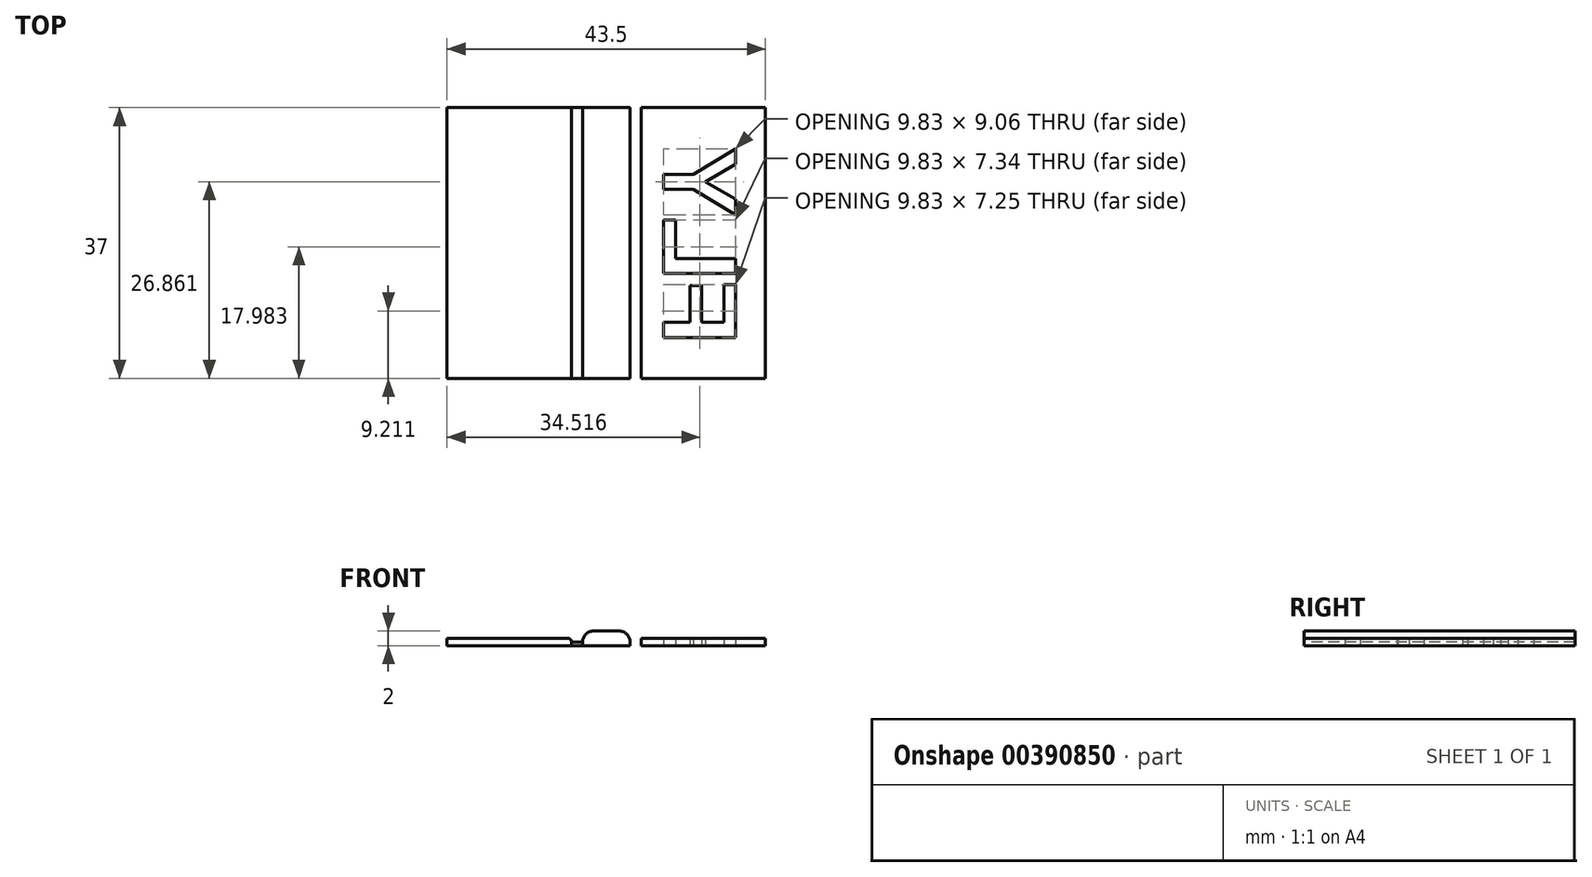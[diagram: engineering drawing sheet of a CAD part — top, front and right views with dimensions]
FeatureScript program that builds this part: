
annotation { "Feature Type Name" : "Feature", "Feature Type Description" : "" }
export const myFeature = defineFeature(function(context is Context, id is Id, definition is map)
    precondition{}
    {
        {
            var Q0;
            Q0=qCreatedBy(makeId("Top.planeOp"),FACE);
            var sketch = newSketch(context, id + "F0", { "sketchPlane" : qUnion([Q0])});
            skLineSegment(sketch, "E0.bottom", {"start": v(-8.5, -18.5) * mm, "end": v(8.5, -18.5) * mm});
            skLineSegment(sketch, "E0.top", {"start": v(-8.5, 18.5) * mm, "end": v(8.5, 18.5) * mm});
            skLineSegment(sketch, "E0.left", {"start": v(-8.5, -18.5) * mm, "end": v(-8.5, 18.5) * mm});
            skLineSegment(sketch, "E0.right", {"start": v(8.5, -18.5) * mm, "end": v(8.5, 18.5) * mm});
            skPoint(sketch, "E0.middle", {"position": v(0, 0) * mm});
            skLineSegment(sketch, "E1.bottom", {"start": v(-8.5, 18.5) * mm, "end": v(-16.5, 18.5) * mm});
            skLineSegment(sketch, "E1.top", {"start": v(-8.5, -18.5) * mm, "end": v(-16.5, -18.5) * mm});
            skLineSegment(sketch, "E1.left", {"start": v(-8.5, 18.5) * mm, "end": v(-8.5, -18.5) * mm});
            skLineSegment(sketch, "E1.right", {"start": v(-16.5, 18.5) * mm, "end": v(-16.5, -18.5) * mm});
            skLineSegment(sketch, "E2", {"start": v(-10, 18.5) * mm, "end": v(-10, -18.5) * mm});
            skLineSegment(sketch, "E3", {"start": v(-16.5, 18.5) * mm, "end": v(-35, 18.5) * mm});
            skLineSegment(sketch, "E4", {"start": v(-35, 18.5) * mm, "end": v(-35, -18.5) * mm});
            skLineSegment(sketch, "E5", {"start": v(-35, -18.5) * mm, "end": v(-16.5, -18.5) * mm});
            skLineSegment(sketch, "E6", {"start": v(-18, 18.5) * mm, "end": v(-18, -18.5) * mm});
            skSolve(sketch);
        }
        {
            var Q0;
            Q0=makeQuery(id+"F0.imprint","IMPRINT",FACE,{"disambiguationData":[TD([[makeQuery(id+"F0.imprint","IMPRINT",EDGE,{"derivedFrom":sQuery(id+"F0.wireOp",EDGE,"E0.bottom")}),1.0]])]});
            var Q1;
            {var subQ0=sQuery(id+"F0.wireOp",EDGE,"E4");Q1=makeQuery(id+"F0.imprint","IMPRINT",FACE,{"disambiguationData":[TD([[makeQuery(id+"F0.imprint","IMPRINT",EDGE,{"derivedFrom":subQ0}),1.0]])]});}
            extrude(context, id + "F1", {"entities" : qUnion([Q0, Q1]), "depth" : 1 * mm, "offsetDistance" : 25 * mm});
        }
        {
            var Q0;
            {var subQ0=sQuery(id+"F0.wireOp",EDGE,"E1.right");Q0=makeQuery(id+"F0.imprint","IMPRINT",FACE,{"disambiguationData":[TD([[makeQuery(id+"F0.imprint","IMPRINT",EDGE,{"derivedFrom":subQ0}),1.0]])]});}
            extrude(context, id + "F2", {"entities" : qUnion([Q0]), "depth" : 2 * mm, "offsetDistance" : 25 * mm});
        }
        {
            var Q0;
            {var subQ0=sQuery(id+"F0.wireOp",EDGE,"E1.right");Q0=makeQuery(id+"F0.imprint","IMPRINT",FACE,{"disambiguationData":[TD([[makeQuery(id+"F0.imprint","IMPRINT",EDGE,{"derivedFrom":subQ0}),-1.0]])]});}
            var Q1;
            {var subQ0=sQuery(id+"F0.wireOp",EDGE,"E1.left");Q1=makeQuery(id+"F0.imprint","IMPRINT",FACE,{"disambiguationData":[TD([[makeQuery(id+"F0.imprint","IMPRINT",EDGE,{"derivedFrom":subQ0}),-1.0]])]});}
            extrude(context, id + "F3", {"entities" : qUnion([Q0, Q1]), "depth" : .5 * mm, "offsetDistance" : 25 * mm});
        }
        {
            var Q0;
            Q0=makeQuery(id+"F2.opExtrude","CAP_EDGE",EDGE,{"disambiguationData":[OSD([sQuery(id+"F0.wireOp",EDGE,"E2")])],"isStart":false});
            var Q1;
            Q1=makeQuery(id+"F2.opExtrude","CAP_EDGE",EDGE,{"disambiguationData":[OSD([sQuery(id+"F0.wireOp",EDGE,"E1.right")])],"isStart":false});
            fillet(context, id + "F4", {"entities" : qUnion([Q0, Q1]), "radius" : 1.5 * mm, "tangentPropagation" : true, "allowEdgeOverflow" : false});
        }
        {
            var Q0;
            Q0=makeQuery(id+"F1.opExtrude","CAP_EDGE",EDGE,{"disambiguationData":[OSD([sQuery(id+"F0.wireOp",EDGE,"E6")])],"isStart":false});
            var Q1;
            Q1=makeQuery(id+"F1.opExtrude","CAP_EDGE",EDGE,{"disambiguationData":[OSD([sQuery(id+"F0.wireOp",EDGE,"E1.left")])],"isStart":false});
            fillet(context, id + "F5", {"entities" : qUnion([Q0, Q1]), "radius" : .5 * mm, "tangentPropagation" : true, "allowEdgeOverflow" : false});
        }
        {
            var Q0;
            Q0=makeQuery(id+"F1.opExtrude","CAP_FACE",FACE,{"disambiguationData":[OSD([sQuery(id+"F0.wireOp",EDGE,"E0.bottom"),sQuery(id+"F0.wireOp",EDGE,"E0.top"),sQuery(id+"F0.wireOp",EDGE,"E0.right"),sQuery(id+"F0.wireOp",EDGE,"E1.left")])],"isStart":true});
            var sketch = newSketch(context, id + "F6", { "sketchPlane" : qUnion([Q0])});
            skText(sketch, "E7", { "text": "FLY", "fontName": "Arimo-Bold.ttf"});
            const initialGuessF6  = {"E7": [-0.0054, 0.01387, 0, -1, 0.01029]};
            skSetInitialGuess(sketch, initialGuessF6);
            skSolve(sketch);
        }
        {
            var Q0;
            Q0 = qSketchRegion(id + "F6", true);
            extrude(context, id + "F7", {"entities" : qUnion([Q0]), "operationType" : NewBodyOperationType.REMOVE, "oppositeDirection" : true, "depth" : 25 * mm, "offsetDistance" : 25 * mm});
        }
    });
